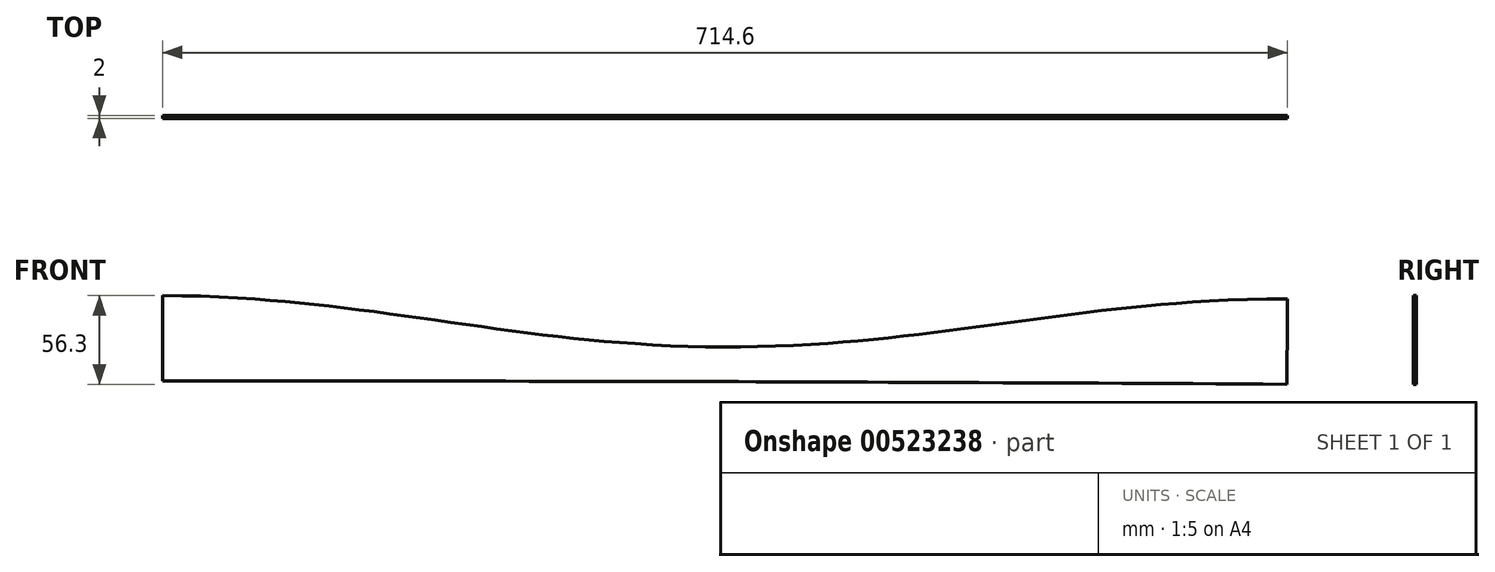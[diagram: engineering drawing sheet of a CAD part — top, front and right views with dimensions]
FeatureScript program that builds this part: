
annotation { "Feature Type Name" : "Feature", "Feature Type Description" : "" }
export const myFeature = defineFeature(function(context is Context, id is Id, definition is map)
    precondition{}
    {
        {
            var Q0;
            Q0=qCreatedBy(makeId("Front.planeOp"),FACE);
            var sketch = newSketch(context, id + "F0", { "sketchPlane" : qUnion([Q0])});
            skLineSegment(sketch, "E0", {"start": v(357.21, -28.4) * mm, "end": v(341.53, -28.3) * mm});
            skLineSegment(sketch, "E1", {"start": v(341.53, -28.3) * mm, "end": v(326.81, -28.22) * mm});
            skLineSegment(sketch, "E2", {"start": v(326.81, -28.22) * mm, "end": v(311.97, -28.14) * mm});
            skLineSegment(sketch, "E3", {"start": v(311.97, -28.14) * mm, "end": v(297.1, -28.06) * mm});
            skLineSegment(sketch, "E4", {"start": v(297.1, -28.06) * mm, "end": v(282.19, -27.97) * mm});
            skLineSegment(sketch, "E5", {"start": v(282.19, -27.97) * mm, "end": v(267.22, -27.9) * mm});
            skLineSegment(sketch, "E6", {"start": v(267.22, -27.9) * mm, "end": v(252.25, -27.81) * mm});
            skLineSegment(sketch, "E7", {"start": v(252.25, -27.81) * mm, "end": v(237.13, -27.74) * mm});
            skLineSegment(sketch, "E8", {"start": v(237.13, -27.74) * mm, "end": v(222.09, -27.67) * mm});
            skLineSegment(sketch, "E9", {"start": v(222.09, -27.67) * mm, "end": v(206.92, -27.6) * mm});
            skLineSegment(sketch, "E10", {"start": v(206.92, -27.6) * mm, "end": v(191.75, -27.53) * mm});
            skLineSegment(sketch, "E11", {"start": v(191.75, -27.53) * mm, "end": v(176.55, -27.46) * mm});
            skLineSegment(sketch, "E12", {"start": v(176.55, -27.46) * mm, "end": v(161.4, -27.4) * mm});
            skLineSegment(sketch, "E13", {"start": v(161.4, -27.4) * mm, "end": v(146.5, -27.34) * mm});
            skLineSegment(sketch, "E14", {"start": v(146.5, -27.34) * mm, "end": v(131.92, -27.28) * mm});
            skLineSegment(sketch, "E15", {"start": v(131.92, -27.28) * mm, "end": v(117.65, -27.22) * mm});
            skLineSegment(sketch, "E16", {"start": v(117.65, -27.22) * mm, "end": v(103.76, -27.16) * mm});
            skLineSegment(sketch, "E17", {"start": v(103.76, -27.16) * mm, "end": v(90.4, -27.11) * mm});
            skLineSegment(sketch, "E18", {"start": v(90.4, -27.11) * mm, "end": v(77.62, -27.06) * mm});
            skLineSegment(sketch, "E19", {"start": v(77.62, -27.06) * mm, "end": v(65.37, -27) * mm});
            skLineSegment(sketch, "E20", {"start": v(65.37, -27) * mm, "end": v(53.52, -26.95) * mm});
            skLineSegment(sketch, "E21", {"start": v(53.52, -26.95) * mm, "end": v(42, -26.9) * mm});
            skLineSegment(sketch, "E22", {"start": v(42, -26.9) * mm, "end": v(30.74, -26.87) * mm});
            skLineSegment(sketch, "E23", {"start": v(30.74, -26.87) * mm, "end": v(19.63, -26.83) * mm});
            skLineSegment(sketch, "E24", {"start": v(19.63, -26.83) * mm, "end": v(8.63, -26.8) * mm});
            skLineSegment(sketch, "E25", {"start": v(8.63, -26.8) * mm, "end": v(-2.35, -26.75) * mm});
            skLineSegment(sketch, "E26", {"start": v(-2.35, -26.75) * mm, "end": v(-13.35, -26.72) * mm});
            skLineSegment(sketch, "E27", {"start": v(-13.35, -26.72) * mm, "end": v(-24.4, -26.7) * mm});
            skLineSegment(sketch, "E28", {"start": v(-24.4, -26.7) * mm, "end": v(-35.58, -26.66) * mm});
            skLineSegment(sketch, "E29", {"start": v(-35.58, -26.66) * mm, "end": v(-46.97, -26.64) * mm});
            skLineSegment(sketch, "E30", {"start": v(-46.97, -26.64) * mm, "end": v(-58.66, -26.62) * mm});
            skLineSegment(sketch, "E31", {"start": v(-58.66, -26.62) * mm, "end": v(-70.72, -26.6) * mm});
            skLineSegment(sketch, "E32", {"start": v(-70.72, -26.6) * mm, "end": v(-83.27, -26.58) * mm});
            skLineSegment(sketch, "E33", {"start": v(-83.27, -26.58) * mm, "end": v(-96.39, -26.56) * mm});
            skLineSegment(sketch, "E34", {"start": v(-96.39, -26.56) * mm, "end": v(-110.17, -26.53) * mm});
            skLineSegment(sketch, "E35", {"start": v(-110.17, -26.53) * mm, "end": v(-124.53, -26.5) * mm});
            skLineSegment(sketch, "E36", {"start": v(-124.53, -26.5) * mm, "end": v(-139.25, -26.48) * mm});
            skLineSegment(sketch, "E37", {"start": v(-139.25, -26.48) * mm, "end": v(-154.3, -26.45) * mm});
            skLineSegment(sketch, "E38", {"start": v(-154.3, -26.45) * mm, "end": v(-169.68, -26.43) * mm});
            skLineSegment(sketch, "E39", {"start": v(-169.68, -26.43) * mm, "end": v(-185.25, -26.4) * mm});
            skLineSegment(sketch, "E40", {"start": v(-185.25, -26.4) * mm, "end": v(-200.81, -26.37) * mm});
            skLineSegment(sketch, "E41", {"start": v(-200.81, -26.37) * mm, "end": v(-216.38, -26.35) * mm});
            skLineSegment(sketch, "E42", {"start": v(-216.38, -26.35) * mm, "end": v(-231.95, -26.33) * mm});
            skLineSegment(sketch, "E43", {"start": v(-231.95, -26.33) * mm, "end": v(-247.52, -26.3) * mm});
            skLineSegment(sketch, "E44", {"start": v(-247.52, -26.3) * mm, "end": v(-263.08, -26.28) * mm});
            skLineSegment(sketch, "E45", {"start": v(-263.08, -26.28) * mm, "end": v(-278.65, -26.26) * mm});
            skLineSegment(sketch, "E46", {"start": v(-278.65, -26.26) * mm, "end": v(-294.2, -26.24) * mm});
            skLineSegment(sketch, "E47", {"start": v(-294.2, -26.24) * mm, "end": v(-309.77, -26.23) * mm});
            skLineSegment(sketch, "E48", {"start": v(-309.77, -26.23) * mm, "end": v(-325.34, -26.22) * mm});
            skLineSegment(sketch, "E49", {"start": v(-325.34, -26.22) * mm, "end": v(-340.9, -26.22) * mm});
            skLineSegment(sketch, "E50", {"start": v(-340.9, -26.22) * mm, "end": v(-357.55, -26.22) * mm});
            skLineSegment(sketch, "E51", {"start": v(-357.55, -26.22) * mm, "end": v(-357.55, -11.28) * mm});
            skLineSegment(sketch, "E52", {"start": v(-357.55, -11.28) * mm, "end": v(-357.55, 2.61) * mm});
            skLineSegment(sketch, "E53", {"start": v(-357.55, 2.61) * mm, "end": v(-357.55, 15.74) * mm});
            skLineSegment(sketch, "E54", {"start": v(-357.55, 15.74) * mm, "end": v(-357.55, 28.4) * mm});
            skLineSegment(sketch, "E55", {"start": v(-357.55, 28.4) * mm, "end": v(-344.74, 28.28) * mm});
            skLineSegment(sketch, "E56", {"start": v(-344.74, 28.28) * mm, "end": v(-332.91, 27.99) * mm});
            skLineSegment(sketch, "E57", {"start": v(-332.91, 27.99) * mm, "end": v(-321.18, 27.53) * mm});
            skLineSegment(sketch, "E58", {"start": v(-321.18, 27.53) * mm, "end": v(-309.42, 26.91) * mm});
            skLineSegment(sketch, "E59", {"start": v(-309.42, 26.91) * mm, "end": v(-298.43, 26.2) * mm});
            skLineSegment(sketch, "E60", {"start": v(-298.43, 26.2) * mm, "end": v(-288.75, 25.44) * mm});
            skLineSegment(sketch, "E61", {"start": v(-288.75, 25.44) * mm, "end": v(-279.43, 24.63) * mm});
            skLineSegment(sketch, "E62", {"start": v(-279.43, 24.63) * mm, "end": v(-270.17, 23.75) * mm});
            skLineSegment(sketch, "E63", {"start": v(-270.17, 23.75) * mm, "end": v(-260.77, 22.77) * mm});
            skLineSegment(sketch, "E64", {"start": v(-260.77, 22.77) * mm, "end": v(-251.3, 21.71) * mm});
            skLineSegment(sketch, "E65", {"start": v(-251.3, 21.71) * mm, "end": v(-241.86, 20.6) * mm});
            skLineSegment(sketch, "E66", {"start": v(-241.86, 20.6) * mm, "end": v(-232.25, 19.4) * mm});
            skLineSegment(sketch, "E67", {"start": v(-232.25, 19.4) * mm, "end": v(-222.67, 18.15) * mm});
            skLineSegment(sketch, "E68", {"start": v(-222.67, 18.15) * mm, "end": v(-213.06, 16.86) * mm});
            skLineSegment(sketch, "E69", {"start": v(-213.06, 16.86) * mm, "end": v(-203.34, 15.53) * mm});
            skLineSegment(sketch, "E70", {"start": v(-203.34, 15.53) * mm, "end": v(-193.76, 14.18) * mm});
            skLineSegment(sketch, "E71", {"start": v(-193.76, 14.18) * mm, "end": v(-183.96, 12.8) * mm});
            skLineSegment(sketch, "E72", {"start": v(-183.96, 12.8) * mm, "end": v(-174.14, 11.4) * mm});
            skLineSegment(sketch, "E73", {"start": v(-174.14, 11.4) * mm, "end": v(-164.5, 10.03) * mm});
            skLineSegment(sketch, "E74", {"start": v(-164.5, 10.03) * mm, "end": v(-154.69, 8.66) * mm});
            skLineSegment(sketch, "E75", {"start": v(-154.69, 8.66) * mm, "end": v(-144.93, 7.31) * mm});
            skLineSegment(sketch, "E76", {"start": v(-144.93, 7.31) * mm, "end": v(-135.23, 6) * mm});
            skLineSegment(sketch, "E77", {"start": v(-135.23, 6) * mm, "end": v(-125.4, 4.73) * mm});
            skLineSegment(sketch, "E78", {"start": v(-125.4, 4.73) * mm, "end": v(-115.7, 3.53) * mm});
            skLineSegment(sketch, "E79", {"start": v(-115.7, 3.53) * mm, "end": v(-105.95, 2.38) * mm});
            skLineSegment(sketch, "E80", {"start": v(-105.95, 2.38) * mm, "end": v(-96.12, 1.3) * mm});
            skLineSegment(sketch, "E81", {"start": v(-96.12, 1.3) * mm, "end": v(-86.45, 0.3) * mm});
            skLineSegment(sketch, "E82", {"start": v(-86.45, 0.3) * mm, "end": v(-76.71, -0.61) * mm});
            skLineSegment(sketch, "E83", {"start": v(-76.71, -0.61) * mm, "end": v(-66.98, -1.43) * mm});
            skLineSegment(sketch, "E84", {"start": v(-66.98, -1.43) * mm, "end": v(-57, -2.18) * mm});
            skLineSegment(sketch, "E85", {"start": v(-57, -2.18) * mm, "end": v(-46.03, -2.87) * mm});
            skLineSegment(sketch, "E86", {"start": v(-46.03, -2.87) * mm, "end": v(-34.56, -3.45) * mm});
            skLineSegment(sketch, "E87", {"start": v(-34.56, -3.45) * mm, "end": v(-23.34, -3.87) * mm});
            skLineSegment(sketch, "E88", {"start": v(-23.34, -3.87) * mm, "end": v(-12.26, -4.14) * mm});
            skLineSegment(sketch, "E89", {"start": v(-12.26, -4.14) * mm, "end": v(-1.24, -4.26) * mm});
            skLineSegment(sketch, "E90", {"start": v(-1.24, -4.26) * mm, "end": v(9.76, -4.24) * mm});
            skLineSegment(sketch, "E91", {"start": v(9.76, -4.24) * mm, "end": v(20.81, -4.07) * mm});
            skLineSegment(sketch, "E92", {"start": v(20.81, -4.07) * mm, "end": v(31.99, -3.75) * mm});
            skLineSegment(sketch, "E93", {"start": v(31.99, -3.75) * mm, "end": v(43.37, -3.27) * mm});
            skLineSegment(sketch, "E94", {"start": v(43.37, -3.27) * mm, "end": v(54.77, -2.65) * mm});
            skLineSegment(sketch, "E95", {"start": v(54.77, -2.65) * mm, "end": v(65.3, -1.94) * mm});
            skLineSegment(sketch, "E96", {"start": v(65.3, -1.94) * mm, "end": v(74.9, -1.2) * mm});
            skLineSegment(sketch, "E97", {"start": v(74.9, -1.2) * mm, "end": v(84.55, -0.37) * mm});
            skLineSegment(sketch, "E98", {"start": v(84.55, -0.37) * mm, "end": v(94.24, 0.55) * mm});
            skLineSegment(sketch, "E99", {"start": v(94.24, 0.55) * mm, "end": v(103.8, 1.54) * mm});
            skLineSegment(sketch, "E100", {"start": v(103.8, 1.54) * mm, "end": v(113.48, 2.6) * mm});
            skLineSegment(sketch, "E101", {"start": v(113.48, 2.6) * mm, "end": v(123.09, 3.74) * mm});
            skLineSegment(sketch, "E102", {"start": v(123.09, 3.74) * mm, "end": v(132.8, 4.93) * mm});
            skLineSegment(sketch, "E103", {"start": v(132.8, 4.93) * mm, "end": v(142.53, 6.16) * mm});
            skLineSegment(sketch, "E104", {"start": v(142.53, 6.16) * mm, "end": v(152.15, 7.42) * mm});
            skLineSegment(sketch, "E105", {"start": v(152.15, 7.42) * mm, "end": v(161.91, 8.73) * mm});
            skLineSegment(sketch, "E106", {"start": v(161.91, 8.73) * mm, "end": v(171.61, 10.04) * mm});
            skLineSegment(sketch, "E107", {"start": v(171.61, 10.04) * mm, "end": v(181.28, 11.35) * mm});
            skLineSegment(sketch, "E108", {"start": v(181.28, 11.35) * mm, "end": v(191.04, 12.68) * mm});
            skLineSegment(sketch, "E109", {"start": v(191.04, 12.68) * mm, "end": v(200.69, 13.97) * mm});
            skLineSegment(sketch, "E110", {"start": v(200.69, 13.97) * mm, "end": v(210.32, 15.25) * mm});
            skLineSegment(sketch, "E111", {"start": v(210.32, 15.25) * mm, "end": v(219.99, 16.5) * mm});
            skLineSegment(sketch, "E112", {"start": v(219.99, 16.5) * mm, "end": v(229.57, 17.7) * mm});
            skLineSegment(sketch, "E113", {"start": v(229.57, 17.7) * mm, "end": v(239.13, 18.84) * mm});
            skLineSegment(sketch, "E114", {"start": v(239.13, 18.84) * mm, "end": v(248.66, 19.92) * mm});
            skLineSegment(sketch, "E115", {"start": v(248.66, 19.92) * mm, "end": v(258.12, 20.94) * mm});
            skLineSegment(sketch, "E116", {"start": v(258.12, 20.94) * mm, "end": v(267.57, 21.87) * mm});
            skLineSegment(sketch, "E117", {"start": v(267.57, 21.87) * mm, "end": v(277.03, 22.73) * mm});
            skLineSegment(sketch, "E118", {"start": v(277.03, 22.73) * mm, "end": v(286.57, 23.52) * mm});
            skLineSegment(sketch, "E119", {"start": v(286.57, 23.52) * mm, "end": v(296.77, 24.25) * mm});
            skLineSegment(sketch, "E120", {"start": v(296.77, 24.25) * mm, "end": v(307.82, 24.94) * mm});
            skLineSegment(sketch, "E121", {"start": v(307.82, 24.94) * mm, "end": v(319.48, 25.5) * mm});
            skLineSegment(sketch, "E122", {"start": v(319.48, 25.5) * mm, "end": v(331.7, 25.92) * mm});
            skLineSegment(sketch, "E123", {"start": v(331.7, 25.92) * mm, "end": v(344.12, 26.16) * mm});
            skLineSegment(sketch, "E124", {"start": v(344.12, 26.16) * mm, "end": v(357.55, 26.21) * mm});
            skLineSegment(sketch, "E125", {"start": v(357.55, 26.21) * mm, "end": v(357.48, 13.5) * mm});
            skLineSegment(sketch, "E126", {"start": v(357.48, 13.5) * mm, "end": v(357.4, 0.34) * mm});
            skLineSegment(sketch, "E127", {"start": v(357.4, 0.34) * mm, "end": v(357.3, -13.52) * mm});
            skLineSegment(sketch, "E128", {"start": v(357.3, -13.52) * mm, "end": v(357.21, -28.4) * mm});
            skLineSegment(sketch, "E129", {"start": v(356.97, -28.15) * mm, "end": v(341.53, -28.06) * mm});
            skLineSegment(sketch, "E130", {"start": v(341.53, -28.06) * mm, "end": v(326.81, -27.97) * mm});
            skLineSegment(sketch, "E131", {"start": v(326.81, -27.97) * mm, "end": v(311.97, -27.89) * mm});
            skLineSegment(sketch, "E132", {"start": v(311.97, -27.89) * mm, "end": v(297.1, -27.8) * mm});
            skLineSegment(sketch, "E133", {"start": v(297.1, -27.8) * mm, "end": v(282.19, -27.72) * mm});
            skLineSegment(sketch, "E134", {"start": v(282.19, -27.72) * mm, "end": v(267.22, -27.64) * mm});
            skLineSegment(sketch, "E135", {"start": v(267.22, -27.64) * mm, "end": v(252.25, -27.56) * mm});
            skLineSegment(sketch, "E136", {"start": v(252.25, -27.56) * mm, "end": v(237.13, -27.5) * mm});
            skLineSegment(sketch, "E137", {"start": v(237.13, -27.5) * mm, "end": v(222.1, -27.42) * mm});
            skLineSegment(sketch, "E138", {"start": v(222.1, -27.42) * mm, "end": v(206.92, -27.35) * mm});
            skLineSegment(sketch, "E139", {"start": v(206.92, -27.35) * mm, "end": v(191.75, -27.28) * mm});
            skLineSegment(sketch, "E140", {"start": v(191.75, -27.28) * mm, "end": v(176.55, -27.21) * mm});
            skLineSegment(sketch, "E141", {"start": v(176.55, -27.21) * mm, "end": v(161.4, -27.15) * mm});
            skLineSegment(sketch, "E142", {"start": v(161.4, -27.15) * mm, "end": v(146.5, -27.09) * mm});
            skLineSegment(sketch, "E143", {"start": v(146.5, -27.09) * mm, "end": v(131.92, -27.03) * mm});
            skLineSegment(sketch, "E144", {"start": v(131.92, -27.03) * mm, "end": v(117.65, -26.97) * mm});
            skLineSegment(sketch, "E145", {"start": v(117.65, -26.97) * mm, "end": v(103.76, -26.91) * mm});
            skLineSegment(sketch, "E146", {"start": v(103.76, -26.91) * mm, "end": v(90.4, -26.86) * mm});
            skLineSegment(sketch, "E147", {"start": v(90.4, -26.86) * mm, "end": v(77.62, -26.81) * mm});
            skLineSegment(sketch, "E148", {"start": v(77.62, -26.81) * mm, "end": v(65.37, -26.76) * mm});
            skLineSegment(sketch, "E149", {"start": v(65.37, -26.76) * mm, "end": v(53.52, -26.7) * mm});
            skLineSegment(sketch, "E150", {"start": v(53.52, -26.7) * mm, "end": v(42, -26.66) * mm});
            skLineSegment(sketch, "E151", {"start": v(42, -26.66) * mm, "end": v(30.74, -26.62) * mm});
            skLineSegment(sketch, "E152", {"start": v(30.74, -26.62) * mm, "end": v(19.63, -26.58) * mm});
            skLineSegment(sketch, "E153", {"start": v(19.63, -26.58) * mm, "end": v(8.63, -26.54) * mm});
            skLineSegment(sketch, "E154", {"start": v(8.63, -26.54) * mm, "end": v(-2.35, -26.5) * mm});
            skLineSegment(sketch, "E155", {"start": v(-2.35, -26.5) * mm, "end": v(-13.35, -26.47) * mm});
            skLineSegment(sketch, "E156", {"start": v(-13.35, -26.47) * mm, "end": v(-24.4, -26.44) * mm});
            skLineSegment(sketch, "E157", {"start": v(-24.4, -26.44) * mm, "end": v(-35.58, -26.41) * mm});
            skLineSegment(sketch, "E158", {"start": v(-35.58, -26.41) * mm, "end": v(-46.97, -26.4) * mm});
            skLineSegment(sketch, "E159", {"start": v(-46.97, -26.4) * mm, "end": v(-58.66, -26.37) * mm});
            skLineSegment(sketch, "E160", {"start": v(-58.66, -26.37) * mm, "end": v(-70.72, -26.35) * mm});
            skLineSegment(sketch, "E161", {"start": v(-70.72, -26.35) * mm, "end": v(-83.27, -26.33) * mm});
            skLineSegment(sketch, "E162", {"start": v(-83.27, -26.33) * mm, "end": v(-96.39, -26.3) * mm});
            skLineSegment(sketch, "E163", {"start": v(-96.39, -26.3) * mm, "end": v(-110.17, -26.28) * mm});
            skLineSegment(sketch, "E164", {"start": v(-110.17, -26.28) * mm, "end": v(-124.53, -26.26) * mm});
            skLineSegment(sketch, "E165", {"start": v(-124.53, -26.26) * mm, "end": v(-139.25, -26.23) * mm});
            skLineSegment(sketch, "E166", {"start": v(-139.25, -26.23) * mm, "end": v(-154.3, -26.2) * mm});
            skLineSegment(sketch, "E167", {"start": v(-154.3, -26.2) * mm, "end": v(-169.68, -26.18) * mm});
            skLineSegment(sketch, "E168", {"start": v(-169.68, -26.18) * mm, "end": v(-185.25, -26.15) * mm});
            skLineSegment(sketch, "E169", {"start": v(-185.25, -26.15) * mm, "end": v(-200.81, -26.12) * mm});
            skLineSegment(sketch, "E170", {"start": v(-200.81, -26.12) * mm, "end": v(-216.38, -26.1) * mm});
            skLineSegment(sketch, "E171", {"start": v(-216.38, -26.1) * mm, "end": v(-231.95, -26.08) * mm});
            skLineSegment(sketch, "E172", {"start": v(-231.95, -26.08) * mm, "end": v(-247.52, -26.06) * mm});
            skLineSegment(sketch, "E173", {"start": v(-247.52, -26.06) * mm, "end": v(-263.08, -26.03) * mm});
            skLineSegment(sketch, "E174", {"start": v(-263.08, -26.03) * mm, "end": v(-278.65, -26.01) * mm});
            skLineSegment(sketch, "E175", {"start": v(-278.65, -26.01) * mm, "end": v(-294.2, -26) * mm});
            skLineSegment(sketch, "E176", {"start": v(-294.2, -26) * mm, "end": v(-309.77, -25.98) * mm});
            skLineSegment(sketch, "E177", {"start": v(-309.77, -25.98) * mm, "end": v(-325.34, -25.97) * mm});
            skLineSegment(sketch, "E178", {"start": v(-325.34, -25.97) * mm, "end": v(-340.9, -25.97) * mm});
            skLineSegment(sketch, "E179", {"start": v(-340.9, -25.97) * mm, "end": v(-357.3, -25.97) * mm});
            skLineSegment(sketch, "E180", {"start": v(-357.3, -25.97) * mm, "end": v(-357.3, -11.28) * mm});
            skLineSegment(sketch, "E181", {"start": v(-357.3, -11.28) * mm, "end": v(-357.3, 2.61) * mm});
            skLineSegment(sketch, "E182", {"start": v(-357.3, 2.61) * mm, "end": v(-357.3, 15.74) * mm});
            skLineSegment(sketch, "E183", {"start": v(-357.3, 15.74) * mm, "end": v(-357.3, 28.15) * mm});
            skLineSegment(sketch, "E184", {"start": v(-357.3, 28.15) * mm, "end": v(-344.74, 28.03) * mm});
            skLineSegment(sketch, "E185", {"start": v(-344.74, 28.03) * mm, "end": v(-332.92, 27.74) * mm});
            skLineSegment(sketch, "E186", {"start": v(-332.92, 27.74) * mm, "end": v(-321.2, 27.28) * mm});
            skLineSegment(sketch, "E187", {"start": v(-321.2, 27.28) * mm, "end": v(-309.43, 26.66) * mm});
            skLineSegment(sketch, "E188", {"start": v(-309.43, 26.66) * mm, "end": v(-298.45, 25.94) * mm});
            skLineSegment(sketch, "E189", {"start": v(-298.45, 25.94) * mm, "end": v(-288.77, 25.2) * mm});
            skLineSegment(sketch, "E190", {"start": v(-288.77, 25.2) * mm, "end": v(-279.45, 24.38) * mm});
            skLineSegment(sketch, "E191", {"start": v(-279.45, 24.38) * mm, "end": v(-270.2, 23.5) * mm});
            skLineSegment(sketch, "E192", {"start": v(-270.2, 23.5) * mm, "end": v(-260.8, 22.52) * mm});
            skLineSegment(sketch, "E193", {"start": v(-260.8, 22.52) * mm, "end": v(-251.32, 21.47) * mm});
            skLineSegment(sketch, "E194", {"start": v(-251.32, 21.47) * mm, "end": v(-241.9, 20.35) * mm});
            skLineSegment(sketch, "E195", {"start": v(-241.9, 20.35) * mm, "end": v(-232.28, 19.15) * mm});
            skLineSegment(sketch, "E196", {"start": v(-232.28, 19.15) * mm, "end": v(-222.7, 17.9) * mm});
            skLineSegment(sketch, "E197", {"start": v(-222.7, 17.9) * mm, "end": v(-213.1, 16.62) * mm});
            skLineSegment(sketch, "E198", {"start": v(-213.1, 16.62) * mm, "end": v(-203.38, 15.28) * mm});
            skLineSegment(sketch, "E199", {"start": v(-203.38, 15.28) * mm, "end": v(-193.8, 13.94) * mm});
            skLineSegment(sketch, "E200", {"start": v(-193.8, 13.94) * mm, "end": v(-184, 12.55) * mm});
            skLineSegment(sketch, "E201", {"start": v(-184, 12.55) * mm, "end": v(-174.18, 11.15) * mm});
            skLineSegment(sketch, "E202", {"start": v(-174.18, 11.15) * mm, "end": v(-164.54, 9.79) * mm});
            skLineSegment(sketch, "E203", {"start": v(-164.54, 9.79) * mm, "end": v(-154.72, 8.4) * mm});
            skLineSegment(sketch, "E204", {"start": v(-154.72, 8.4) * mm, "end": v(-144.96, 7.06) * mm});
            skLineSegment(sketch, "E205", {"start": v(-144.96, 7.06) * mm, "end": v(-135.26, 5.76) * mm});
            skLineSegment(sketch, "E206", {"start": v(-135.26, 5.76) * mm, "end": v(-125.44, 4.49) * mm});
            skLineSegment(sketch, "E207", {"start": v(-125.44, 4.49) * mm, "end": v(-115.74, 3.28) * mm});
            skLineSegment(sketch, "E208", {"start": v(-115.74, 3.28) * mm, "end": v(-105.98, 2.13) * mm});
            skLineSegment(sketch, "E209", {"start": v(-105.98, 2.13) * mm, "end": v(-96.15, 1.05) * mm});
            skLineSegment(sketch, "E210", {"start": v(-96.15, 1.05) * mm, "end": v(-86.48, 0.05) * mm});
            skLineSegment(sketch, "E211", {"start": v(-86.48, 0.05) * mm, "end": v(-76.73, -0.86) * mm});
            skLineSegment(sketch, "E212", {"start": v(-76.73, -0.86) * mm, "end": v(-67, -1.68) * mm});
            skLineSegment(sketch, "E213", {"start": v(-67, -1.68) * mm, "end": v(-57.02, -2.43) * mm});
            skLineSegment(sketch, "E214", {"start": v(-57.02, -2.43) * mm, "end": v(-46.04, -3.12) * mm});
            skLineSegment(sketch, "E215", {"start": v(-46.04, -3.12) * mm, "end": v(-34.57, -3.7) * mm});
            skLineSegment(sketch, "E216", {"start": v(-34.57, -3.7) * mm, "end": v(-23.35, -4.12) * mm});
            skLineSegment(sketch, "E217", {"start": v(-23.35, -4.12) * mm, "end": v(-12.26, -4.39) * mm});
            skLineSegment(sketch, "E218", {"start": v(-12.26, -4.39) * mm, "end": v(-1.24, -4.51) * mm});
            skLineSegment(sketch, "E219", {"start": v(-1.24, -4.51) * mm, "end": v(9.76, -4.5) * mm});
            skLineSegment(sketch, "E220", {"start": v(9.76, -4.5) * mm, "end": v(20.82, -4.32) * mm});
            skLineSegment(sketch, "E221", {"start": v(20.82, -4.32) * mm, "end": v(32, -4) * mm});
            skLineSegment(sketch, "E222", {"start": v(32, -4) * mm, "end": v(43.38, -3.52) * mm});
            skLineSegment(sketch, "E223", {"start": v(43.38, -3.52) * mm, "end": v(54.79, -2.9) * mm});
            skLineSegment(sketch, "E224", {"start": v(54.79, -2.9) * mm, "end": v(65.33, -2.2) * mm});
            skLineSegment(sketch, "E225", {"start": v(65.33, -2.2) * mm, "end": v(74.92, -1.45) * mm});
            skLineSegment(sketch, "E226", {"start": v(74.92, -1.45) * mm, "end": v(84.57, -0.62) * mm});
            skLineSegment(sketch, "E227", {"start": v(84.57, -0.62) * mm, "end": v(94.26, 0.3) * mm});
            skLineSegment(sketch, "E228", {"start": v(94.26, 0.3) * mm, "end": v(103.83, 1.29) * mm});
            skLineSegment(sketch, "E229", {"start": v(103.83, 1.29) * mm, "end": v(113.51, 2.36) * mm});
            skLineSegment(sketch, "E230", {"start": v(113.51, 2.36) * mm, "end": v(123.12, 3.49) * mm});
            skLineSegment(sketch, "E231", {"start": v(123.12, 3.49) * mm, "end": v(132.82, 4.68) * mm});
            skLineSegment(sketch, "E232", {"start": v(132.82, 4.68) * mm, "end": v(142.56, 5.92) * mm});
            skLineSegment(sketch, "E233", {"start": v(142.56, 5.92) * mm, "end": v(152.18, 7.17) * mm});
            skLineSegment(sketch, "E234", {"start": v(152.18, 7.17) * mm, "end": v(161.95, 8.48) * mm});
            skLineSegment(sketch, "E235", {"start": v(161.95, 8.48) * mm, "end": v(171.64, 9.8) * mm});
            skLineSegment(sketch, "E236", {"start": v(171.64, 9.8) * mm, "end": v(181.31, 11.1) * mm});
            skLineSegment(sketch, "E237", {"start": v(181.31, 11.1) * mm, "end": v(191.08, 12.43) * mm});
            skLineSegment(sketch, "E238", {"start": v(191.08, 12.43) * mm, "end": v(200.72, 13.73) * mm});
            skLineSegment(sketch, "E239", {"start": v(200.72, 13.73) * mm, "end": v(210.35, 15) * mm});
            skLineSegment(sketch, "E240", {"start": v(210.35, 15) * mm, "end": v(220.02, 16.25) * mm});
            skLineSegment(sketch, "E241", {"start": v(220.02, 16.25) * mm, "end": v(229.6, 17.45) * mm});
            skLineSegment(sketch, "E242", {"start": v(229.6, 17.45) * mm, "end": v(239.15, 18.59) * mm});
            skLineSegment(sketch, "E243", {"start": v(239.15, 18.59) * mm, "end": v(248.69, 19.67) * mm});
            skLineSegment(sketch, "E244", {"start": v(248.69, 19.67) * mm, "end": v(258.15, 20.69) * mm});
            skLineSegment(sketch, "E245", {"start": v(258.15, 20.69) * mm, "end": v(267.59, 21.62) * mm});
            skLineSegment(sketch, "E246", {"start": v(267.59, 21.62) * mm, "end": v(277.05, 22.48) * mm});
            skLineSegment(sketch, "E247", {"start": v(277.05, 22.48) * mm, "end": v(286.6, 23.27) * mm});
            skLineSegment(sketch, "E248", {"start": v(286.6, 23.27) * mm, "end": v(296.78, 24) * mm});
            skLineSegment(sketch, "E249", {"start": v(296.78, 24) * mm, "end": v(307.83, 24.69) * mm});
            skLineSegment(sketch, "E250", {"start": v(307.83, 24.69) * mm, "end": v(319.5, 25.25) * mm});
            skLineSegment(sketch, "E251", {"start": v(319.5, 25.25) * mm, "end": v(331.7, 25.67) * mm});
            skLineSegment(sketch, "E252", {"start": v(331.7, 25.67) * mm, "end": v(344.12, 25.9) * mm});
            skLineSegment(sketch, "E253", {"start": v(344.12, 25.9) * mm, "end": v(357.3, 25.96) * mm});
            skLineSegment(sketch, "E254", {"start": v(357.3, 25.96) * mm, "end": v(357.23, 13.5) * mm});
            skLineSegment(sketch, "E255", {"start": v(357.23, 13.5) * mm, "end": v(357.14, 0.34) * mm});
            skLineSegment(sketch, "E256", {"start": v(357.14, 0.34) * mm, "end": v(357.06, -13.52) * mm});
            skLineSegment(sketch, "E257", {"start": v(357.06, -13.52) * mm, "end": v(356.97, -28.15) * mm});
            skSolve(sketch);
        }
        {
            var Q0;
            Q0=makeQuery(id+"F0.imprint","IMPRINT",FACE,{"disambiguationData":[TD([[makeQuery(id+"F0.imprint","IMPRINT",EDGE,{"derivedFrom":sQuery(id+"F0.wireOp",EDGE,"E129")}),-1.0]])]});
            extrude(context, id + "F1", {"entities" : qUnion([Q0]), "depth" : 2 * mm, "offsetDistance" : 25 * mm});
        }
    });
